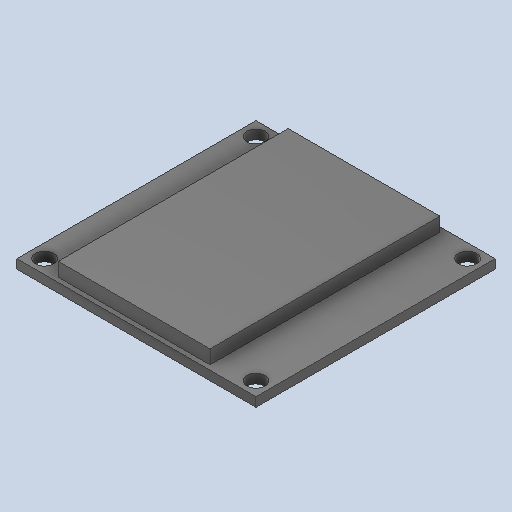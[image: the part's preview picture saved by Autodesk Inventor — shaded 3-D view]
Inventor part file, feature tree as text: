
AUTODESK INVENTOR PART (.ipt)
format: ipt  version: 2025.2 (Build 292293000, 293)  size: 140,800 bytes
history: native  units: mm
features: extrude x2, sketch x2
ambient origin geometry x8: Origin, YZ Plane, XZ Plane, XY Plane, X Axis, Y Axis, Z Axis, Center Point
bodies: Solid1 (feature_tree)
feature tree (4):
  extrude  "Extrusion1"  Depth=26.0mm
  extrude  "Extrusion2"  Depth=1.5mm
  sketch  "Sketch1"  dims[d0=26.0mm d1=26.0mm]
  sketch  "Sketch2"  dims[d2=2.0mm d3=1.5mm d4=1.0mm d5=0.0mm d6=16.5mm d7=25.0mm d8=4.0mm d9=1.5mm d10=0.0mm]
